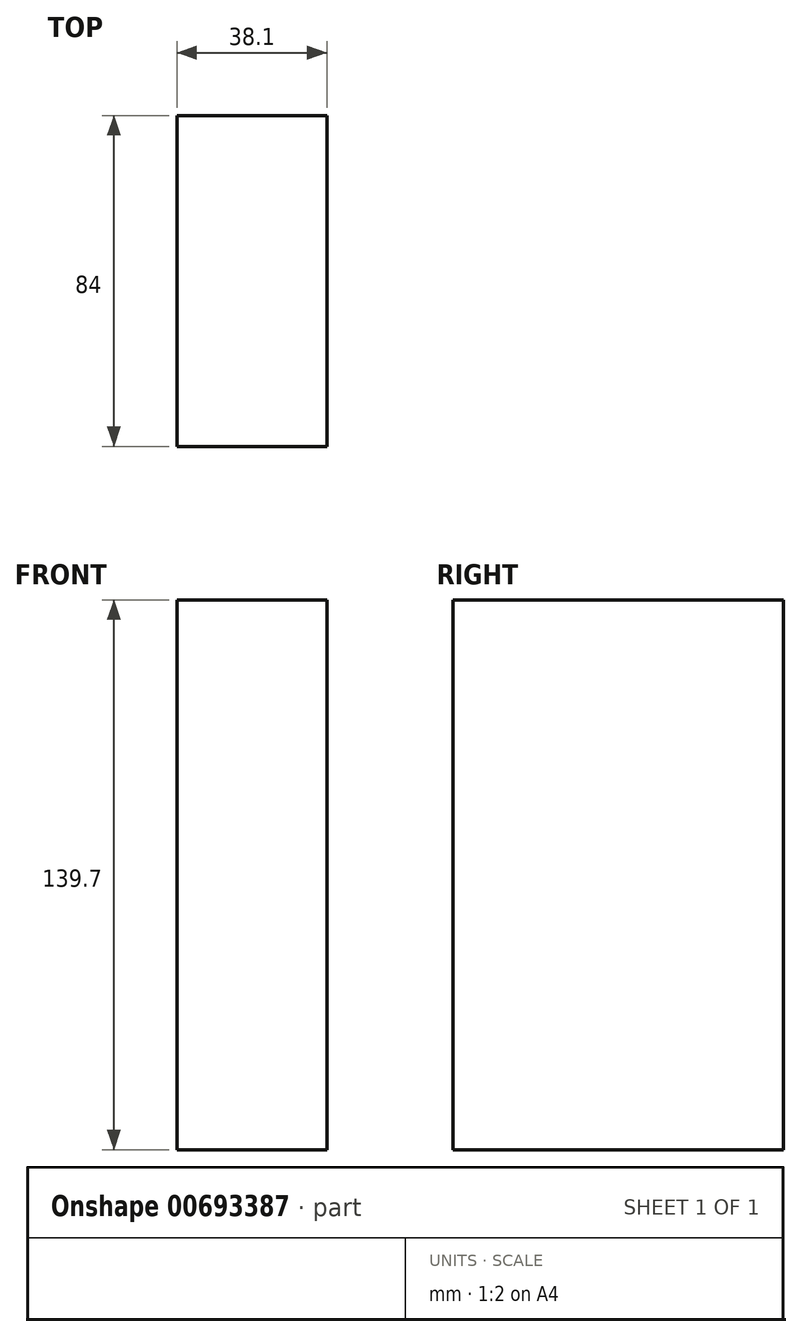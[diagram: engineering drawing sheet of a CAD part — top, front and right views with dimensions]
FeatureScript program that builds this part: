
annotation { "Feature Type Name" : "Feature", "Feature Type Description" : "" }
export const myFeature = defineFeature(function(context is Context, id is Id, definition is map)
    precondition{}
    {
        {
            assignVariable(context, id + "F0", {"name" : "L", "anyValue" : 84});
        }
        {
            var Q0;
            Q0=qCreatedBy(makeId("Front.planeOp"),FACE);
            var sketch = newSketch(context, id + "F1", { "sketchPlane" : qUnion([Q0])});
            skLineSegment(sketch, "E0.bottom", {"start": v(-170.4, 139.7) * mm, "end": v(-132.3, 139.7) * mm});
            skLineSegment(sketch, "E0.top", {"start": v(-170.4, 0) * mm, "end": v(-132.3, 0) * mm});
            skLineSegment(sketch, "E0.left", {"start": v(-170.4, 139.7) * mm, "end": v(-170.4, 0) * mm});
            skLineSegment(sketch, "E0.right", {"start": v(-132.3, 139.7) * mm, "end": v(-132.3, 0) * mm});
            skSolve(sketch);
        }
        {
            var Q0;
            Q0 = qSketchRegion(id + "F1", true);
            extrude(context, id + "F2", {"entities" : qUnion([Q0]), "depth" : (getVariable(context, 'L')) * mm, "offsetDistance" : 25.4 * mm});
        }
    });
